# Revit family: Boiler
name_source: partatom
category: Mechanical Equipment
units: mm (PartAtom-declared; Revit-internal decimal feet)

## family parameters
Always vertical = Yes
Classification Number = 23.75.10.11.14.11
Cut with Voids When Loaded = No
Maintain Annotation Orientation = No
Part Type = Normal
Room Calculation Point = No
Round Connector Dimension = Use Diameter
Shared = No
Work Plane-Based = Yes

## types (1)
- Boiler
    AFUE (%) = 87
    Assembly Code = D3020100
    Case Material = ARCAT - Metal - Aluminum, Painted - Blue
    Construction Details = http://www.arcat.com
    Default Elevation = 4' - 0"
    Description = HVAC Residential Boiler
    Duct Type = ARCAT - Metal - Aluminum
    Expected Lifespan (Years) = 35
    Flue Diameter = 0' - 6"
    Fuel Type = ARCAT - Fuel Oil #2
    Green Building-LEED = http://www.arcat.com
    Keynote = 15500
    Maintenance Schedule (Months) = 12
    Manufacturer = Generic
    Manufacturer Fax = (203) 939-2444
    Manufacturer Website = http://www.arcat.com
    Model = Generic
    Operating Pressure = 120
    Operating Temperature = 160 F
    Product Data = http://www.arcat.com
    Product Properties = http://www.arcat.com
    Specification = http://www.arcat.com
    Warranty Duration (Years) = 10
    Zone Count = 6
    fluerad = 0' - 3"
    risrheight = 0' - 5"

## geometry (parser evidence)
native form markers: Sweep x4
no freeform markers — native parametric forms only
